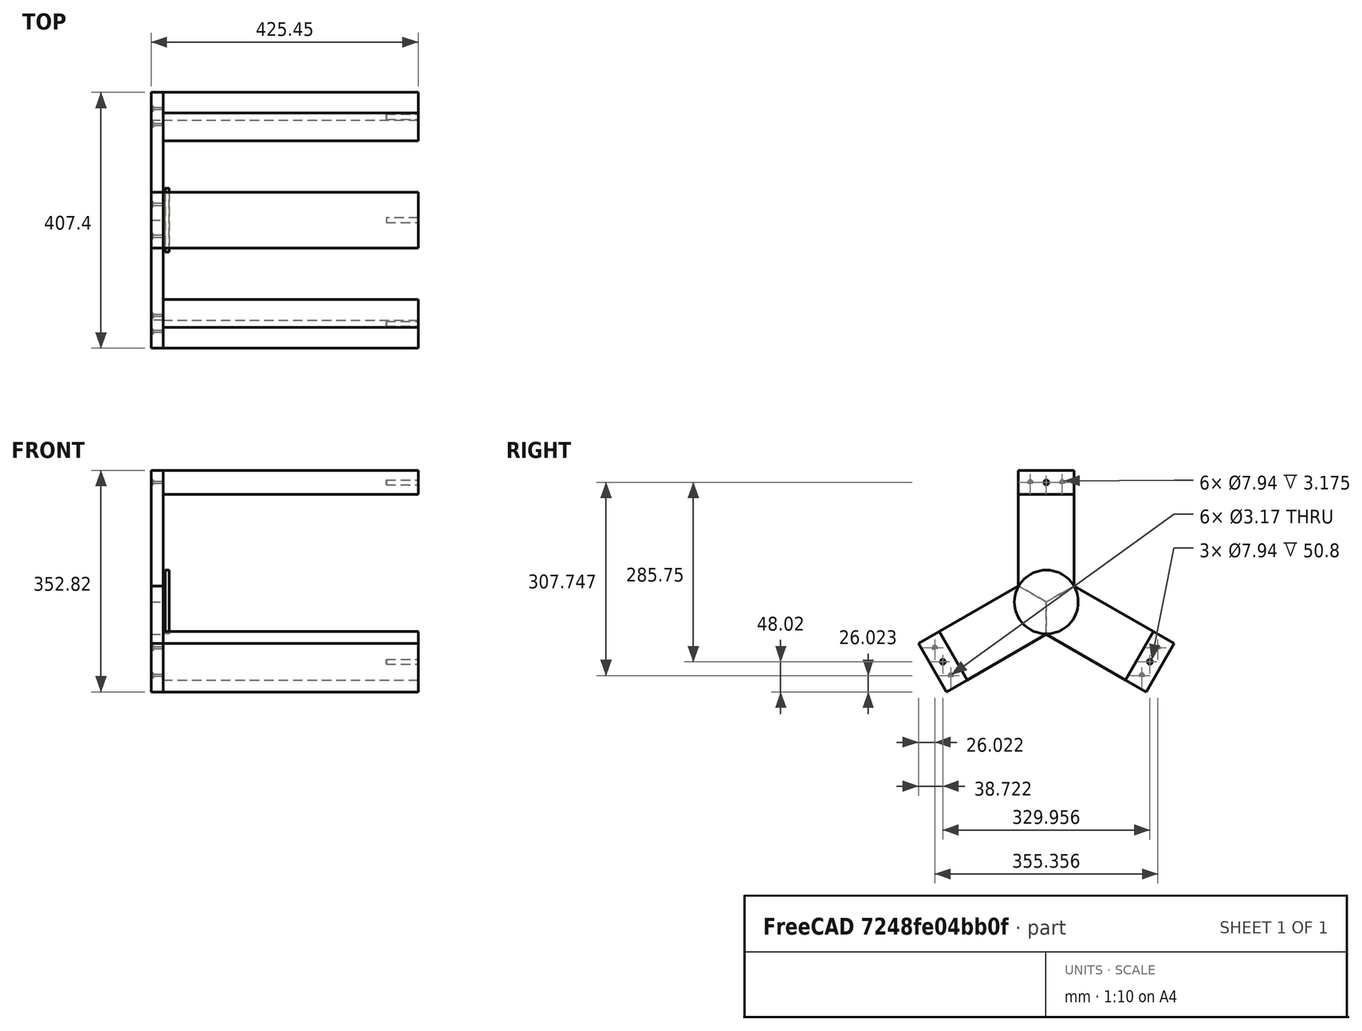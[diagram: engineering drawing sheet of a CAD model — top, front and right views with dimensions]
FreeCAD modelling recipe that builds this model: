
FCSTD DOCUMENT  (FreeCAD 0.20RUnknown)
Label: base
License: All rights reserved
LicenseURL: http://en.wikipedia.org/wiki/All_rights_reserved
objects: Sketcher::SketchObject×19, PartDesign::Pocket×12, PartDesign::Pad×7, PartDesign::Body×7, TechDraw::DrawViewDimension×4, TechDraw::DrawProjGroupItem×2, TechDraw::DrawSVGTemplate×1, TechDraw::DrawProjGroup×1, TechDraw::DrawPage×1, App::Part×1
note: 64 computed .brp shape members not serialized (recipe doc carries the construction recipe); baked Part::Feature solids carry a one-line shape summary decoded from their .brp

FEATURE [Sketcher::SketchObject] Sketch155
  FullyConstrained = true
  MapMode = 5
  Placement = pos=(0,0,0) rot=(0.57735,0.57735,0.57735;2.0944rad)
  Support = -> [YZ_Plane061]
  sketch-geometry (5):
    g0: LineSegment StartX=44.45 StartY=209.55 StartZ=0 EndX=44.45 EndY=171.45 EndZ=0
    g1: LineSegment StartX=44.45 StartY=171.45 StartZ=0 EndX=-44.45 EndY=171.45 EndZ=0
    g2: LineSegment StartX=-44.45 StartY=171.45 StartZ=0 EndX=-44.45 EndY=209.55 EndZ=0
    g3: LineSegment StartX=-44.45 StartY=209.55 StartZ=0 EndX=44.45 EndY=209.55 EndZ=0
    g4: GeomPoint X=0 Y=190.5 Z=0
  constraints (13):
    c: Coincident(g0,g1)
    c: Coincident(g1,g2)
    c: Coincident(g2,g3)
    c: Coincident(g3,g0)
    c: Horizontal(g1)
    c: Horizontal(g3)
    c: Vertical(g0)
    c: Vertical(g2)
    c: Symmetric(g1,g0,g4)
    c: PointOnObject(g4,g-2)
    c: Distance(g-1,g4) = 190.5
    c: DistanceX(g3,g3) = 88.9
    c: DistanceY(g2,g2) = 38.1
FEATURE [PartDesign::Pad] Pad052
  Direction = (1,-2e-16,3e-16)
  Length = 406.4
  Length2 = 10
  Placement = pos=(0,0,0) rot=(0.57735,0.57735,0.57735;2.0944rad)
  Profile = -> Sketch155
  ReferenceAxis = -> Sketch155 [N_Axis]
  Type = 0
FEATURE [Sketcher::SketchObject] Sketch157
  FullyConstrained = true
  MapMode = 5
  Placement = pos=(406.4,-8.9e-14,8.9e-14) rot=(0.57735,0.57735,0.57735;2.0944rad)
  sketch-geometry (1):
    g0: Circle CenterX=0 CenterY=190.5 CenterZ=0 NormalX=0 NormalY=0 NormalZ=1 AngleXU=0 Radius=3.96875
  constraints (3):
    c: PointOnObject(g0,g-2)
    c: DistanceY(g-1,g0) = 190.5
    c: Diameter(g0) = 7.9375
FEATURE [PartDesign::Pocket] Pocket013
  BaseFeature = -> Pad052
  Direction = (-1,2e-16,-2e-16)
  Length = 50.8
  Length2 = 5
  Placement = pos=(0,0,0) rot=(0.57735,0.57735,0.57735;2.0944rad)
  Profile = -> Sketch157
  ReferenceAxis = -> Sketch157 [N_Axis]
  Type = 0
FEATURE [PartDesign::Body] Body050  label="base-leg-001"
  Group = -> [Sketch155,Pad052,Sketch157,Pocket013]
  Origin = -> Origin061
  Placement = pos=(-841.375,0,0) rot=(1,0,0;0rad)
  Tip = -> Pocket013
FEATURE [Sketcher::SketchObject] Sketch158
  FullyConstrained = true
  MapMode = 5
  Placement = pos=(0,0,0) rot=(0.57735,0.57735,0.57735;2.0944rad)
  Support = -> [YZ_Plane061]
  sketch-geometry (5):
    g0: LineSegment StartX=44.45 StartY=209.55 StartZ=0 EndX=44.45 EndY=171.45 EndZ=0
    g1: LineSegment StartX=44.45 StartY=171.45 StartZ=0 EndX=-44.45 EndY=171.45 EndZ=0
    g2: LineSegment StartX=-44.45 StartY=171.45 StartZ=0 EndX=-44.45 EndY=209.55 EndZ=0
    g3: LineSegment StartX=-44.45 StartY=209.55 StartZ=0 EndX=44.45 EndY=209.55 EndZ=0
    g4: GeomPoint X=0 Y=190.5 Z=0
  constraints (13):
    c: Coincident(g0,g1)
    c: Coincident(g1,g2)
    c: Coincident(g2,g3)
    c: Coincident(g3,g0)
    c: Horizontal(g1)
    c: Horizontal(g3)
    c: Vertical(g0)
    c: Vertical(g2)
    c: Symmetric(g1,g0,g4)
    c: PointOnObject(g4,g-2)
    c: Distance(g-1,g4) = 190.5
    c: DistanceX(g3,g3) = 88.9
    c: DistanceY(g2,g2) = 38.1
FEATURE [PartDesign::Pad] Pad053
  Direction = (1,-2e-16,3e-16)
  Length = 406.4
  Length2 = 10
  Placement = pos=(0,0,0) rot=(0.57735,0.57735,0.57735;2.0944rad)
  Profile = -> Sketch158
  ReferenceAxis = -> Sketch158 [N_Axis]
  Type = 0
FEATURE [Sketcher::SketchObject] Sketch159
  FullyConstrained = true
  MapMode = 5
  Placement = pos=(406.4,-8.9e-14,8.9e-14) rot=(0.57735,0.57735,0.57735;2.0944rad)
  sketch-geometry (1):
    g0: Circle CenterX=0 CenterY=190.5 CenterZ=0 NormalX=0 NormalY=0 NormalZ=1 AngleXU=0 Radius=3.96875
  constraints (3):
    c: PointOnObject(g0,g-2)
    c: DistanceY(g-1,g0) = 190.5
    c: Diameter(g0) = 7.9375
FEATURE [PartDesign::Pocket] Pocket014
  BaseFeature = -> Pad053
  Direction = (-1,2e-16,-2e-16)
  Length = 50.8
  Length2 = 5
  Placement = pos=(0,0,0) rot=(0.57735,0.57735,0.57735;2.0944rad)
  Profile = -> Sketch159
  ReferenceAxis = -> Sketch159 [N_Axis]
  Type = 0
FEATURE [PartDesign::Body] Body051  label="base-leg-002"
  Group = -> [Sketch158,Pad053,Sketch159,Pocket014]
  Origin = -> Origin
  Placement = pos=(-841.375,0,0) rot=(1,0,0;4.18879rad)
  Tip = -> Pocket014
FEATURE [Sketcher::SketchObject] Sketch160
  FullyConstrained = true
  MapMode = 5
  Placement = pos=(0,0,0) rot=(0.57735,0.57735,0.57735;2.0944rad)
  Support = -> [YZ_Plane061]
  sketch-geometry (5):
    g0: LineSegment StartX=44.45 StartY=209.55 StartZ=0 EndX=44.45 EndY=171.45 EndZ=0
    g1: LineSegment StartX=44.45 StartY=171.45 StartZ=0 EndX=-44.45 EndY=171.45 EndZ=0
    g2: LineSegment StartX=-44.45 StartY=171.45 StartZ=0 EndX=-44.45 EndY=209.55 EndZ=0
    g3: LineSegment StartX=-44.45 StartY=209.55 StartZ=0 EndX=44.45 EndY=209.55 EndZ=0
    g4: GeomPoint X=0 Y=190.5 Z=0
  constraints (13):
    c: Coincident(g0,g1)
    c: Coincident(g1,g2)
    c: Coincident(g2,g3)
    c: Coincident(g3,g0)
    c: Horizontal(g1)
    c: Horizontal(g3)
    c: Vertical(g0)
    c: Vertical(g2)
    c: Symmetric(g1,g0,g4)
    c: PointOnObject(g4,g-2)
    c: Distance(g-1,g4) = 190.5
    c: DistanceX(g3,g3) = 88.9
    c: DistanceY(g2,g2) = 38.1
FEATURE [PartDesign::Pad] Pad054
  Direction = (1,-2e-16,3e-16)
  Length = 406.4
  Length2 = 10
  Placement = pos=(0,0,0) rot=(0.57735,0.57735,0.57735;2.0944rad)
  Profile = -> Sketch160
  ReferenceAxis = -> Sketch160 [N_Axis]
  Type = 0
FEATURE [Sketcher::SketchObject] Sketch161
  FullyConstrained = true
  MapMode = 5
  Placement = pos=(406.4,-8.9e-14,8.9e-14) rot=(0.57735,0.57735,0.57735;2.0944rad)
  sketch-geometry (1):
    g0: Circle CenterX=0 CenterY=190.5 CenterZ=0 NormalX=0 NormalY=0 NormalZ=1 AngleXU=0 Radius=3.96875
  constraints (3):
    c: PointOnObject(g0,g-2)
    c: DistanceY(g-1,g0) = 190.5
    c: Diameter(g0) = 7.9375
FEATURE [PartDesign::Pocket] Pocket015
  BaseFeature = -> Pad054
  Direction = (-1,2e-16,-2e-16)
  Length = 50.8
  Length2 = 5
  Placement = pos=(0,0,0) rot=(0.57735,0.57735,0.57735;2.0944rad)
  Profile = -> Sketch161
  ReferenceAxis = -> Sketch161 [N_Axis]
  Type = 0
FEATURE [PartDesign::Body] Body052  label="base-leg-003"
  Group = -> [Sketch160,Pad054,Sketch161,Pocket015]
  Origin = -> Origin062
  Placement = pos=(-841.375,0,0) rot=(1,0,0;2.0944rad)
  Tip = -> Pocket015
FEATURE [Sketcher::SketchObject] Sketch
  FullyConstrained = true
  MapMode = 5
  Support = -> [XY_Plane063]
  sketch-geometry (5):
    g0: LineSegment StartX=-9.525 StartY=-44.45 StartZ=0 EndX=-9.525 EndY=44.45 EndZ=0
    g1: LineSegment StartX=-9.525 StartY=44.45 StartZ=0 EndX=9.525 EndY=44.45 EndZ=0
    g2: LineSegment StartX=9.525 StartY=44.45 StartZ=0 EndX=9.525 EndY=-44.45 EndZ=0
    g3: LineSegment StartX=9.525 StartY=-44.45 StartZ=0 EndX=-9.525 EndY=-44.45 EndZ=0
    g4: GeomPoint X=2e-16 Y=-3e-16 Z=0
  constraints (12):
    c: Coincident(g0,g1)
    c: Coincident(g1,g2)
    c: Coincident(g2,g3)
    c: Coincident(g3,g0)
    c: Horizontal(g1)
    c: Horizontal(g3)
    c: Vertical(g0)
    c: Vertical(g2)
    c: Symmetric(g1,g0,g4)
    c: Coincident(g4,g-1)
    c: DistanceY(g2,g2) = 88.9
    c: DistanceX(g3,g3) = 19.05
FEATURE [PartDesign::Pad] Pad
  Direction = (0,0,1)
  Length = 209.55
  Length2 = 10
  Profile = -> Sketch
  ReferenceAxis = -> Sketch [N_Axis]
  Type = 0
FEATURE [Sketcher::SketchObject] Sketch162
  FullyConstrained = true
  MapMode = 5
  Placement = pos=(-9.525,0,0) rot=(0.57735,-0.57735,-0.57735;2.0944rad)
  Support = -> [Pad]
  sketch-geometry (6):
    g0: LineSegment StartX=0 StartY=0 StartZ=0 EndX=44.45 EndY=25.6632 EndZ=0
    g1: LineSegment StartX=0 StartY=0 StartZ=0 EndX=-44.45 EndY=25.6632 EndZ=0
    g2: LineSegment StartX=-44.45 StartY=25.6632 StartZ=0 EndX=44.45 EndY=25.6632 EndZ=0
    g3: LineSegment StartX=44.45 StartY=25.6632 StartZ=0 EndX=44.45 EndY=0 EndZ=0
    g4: LineSegment StartX=44.45 StartY=0 StartZ=0 EndX=-44.45 EndY=0 EndZ=0
    g5: LineSegment StartX=-44.45 StartY=0 StartZ=0 EndX=-44.45 EndY=25.6632 EndZ=0
  constraints (16):
    c: Coincident(g0,g-1)
    c: Coincident(g1,g0)
    c: Angle(g0,g-2) = 1.0472
    c: Angle(g-2,g1) = 1.0472
    c: Coincident(g2,g3)
    c: Coincident(g3,g4)
    c: Coincident(g4,g5)
    c: Coincident(g5,g2)
    c: Horizontal(g2)
    c: Horizontal(g4)
    c: Vertical(g3)
    c: Vertical(g5)
    c: Coincident(g2,g1)
    c: Coincident(g0,g2)
    c: PointOnObject(g3,g-1)
    c: DistanceX(g4,g4) = 88.9
FEATURE [PartDesign::Pocket] Pocket
  BaseFeature = -> Pad
  Direction = (1,0,0)
  Length = 5
  Length2 = 5
  Profile = -> Sketch162
  ReferenceAxis = -> Sketch162 [N_Axis]
  Type = 1
FEATURE [Sketcher::SketchObject] Sketch163
  ExternalGeometry = -> [Pocket]
  FullyConstrained = true
  MapMode = 5
  Placement = pos=(-9.525,0,0) rot=(0.57735,-0.57735,-0.57735;2.0944rad)
  Support = -> [Pocket]
  sketch-geometry (2):
    g0: Circle CenterX=-25.4 CenterY=190.5 CenterZ=0 NormalX=0 NormalY=0 NormalZ=1 AngleXU=0 Radius=1.5875
    g1: Circle CenterX=25.4 CenterY=190.5 CenterZ=0 NormalX=0 NormalY=0 NormalZ=1 AngleXU=0 Radius=1.5875
  constraints (6):
    c: Equal(g1,g0)
    c: DistanceX(g-4,g0) = 19.05
    c: DistanceX(g1,g-5) = 19.05
    c: DistanceY(g1,g-5) = 19.05
    c: DistanceY(g0,g-4) = 19.05
    c: Diameter(g0) = 3.175
FEATURE [PartDesign::Pocket] Pocket016
  BaseFeature = -> Pocket
  Direction = (1,0,0)
  Length = 5
  Length2 = 5
  Profile = -> Sketch163
  ReferenceAxis = -> Sketch163 [N_Axis]
  Type = 1
FEATURE [Sketcher::SketchObject] Sketch164
  ExternalGeometry = -> [Pocket016]
  FullyConstrained = true
  MapMode = 5
  Placement = pos=(-9.525,0,0) rot=(0.57735,-0.57735,-0.57735;2.0944rad)
  Support = -> [Pocket016]
  sketch-geometry (2):
    g0: Circle CenterX=-25.4 CenterY=190.5 CenterZ=0 NormalX=0 NormalY=0 NormalZ=1 AngleXU=0 Radius=3.96875
    g1: Circle CenterX=25.4 CenterY=190.5 CenterZ=0 NormalX=0 NormalY=0 NormalZ=1 AngleXU=0 Radius=3.96875
  constraints (4):
    c: Coincident(g0,g-4)
    c: Coincident(g1,g-3)
    c: Equal(g1,g0)
    c: Diameter(g1) = 7.9375
FEATURE [PartDesign::Pocket] Pocket017
  BaseFeature = -> Pocket016
  Direction = (1,0,0)
  Length = 3.175
  Length2 = 5
  Profile = -> Sketch164
  ReferenceAxis = -> Sketch164 [N_Axis]
  Type = 0
FEATURE [PartDesign::Body] Body  label="base-leg-brace-001"
  Group = -> [Sketch,Pad,Sketch162,Pocket,Sketch163,Pocket016,Sketch164,Pocket017]
  Origin = -> Origin063
  Placement = pos=(-850.9,0,0) rot=(1,0,0;0rad)
  Tip = -> Pocket017
FEATURE [Sketcher::SketchObject] Sketch165
  FullyConstrained = true
  MapMode = 5
  Support = -> [XY_Plane063]
  sketch-geometry (5):
    g0: LineSegment StartX=-9.525 StartY=-44.45 StartZ=0 EndX=-9.525 EndY=44.45 EndZ=0
    g1: LineSegment StartX=-9.525 StartY=44.45 StartZ=0 EndX=9.525 EndY=44.45 EndZ=0
    g2: LineSegment StartX=9.525 StartY=44.45 StartZ=0 EndX=9.525 EndY=-44.45 EndZ=0
    g3: LineSegment StartX=9.525 StartY=-44.45 StartZ=0 EndX=-9.525 EndY=-44.45 EndZ=0
    g4: GeomPoint X=2e-16 Y=-3e-16 Z=0
  constraints (12):
    c: Coincident(g0,g1)
    c: Coincident(g1,g2)
    c: Coincident(g2,g3)
    c: Coincident(g3,g0)
    c: Horizontal(g1)
    c: Horizontal(g3)
    c: Vertical(g0)
    c: Vertical(g2)
    c: Symmetric(g1,g0,g4)
    c: Coincident(g4,g-1)
    c: DistanceY(g2,g2) = 88.9
    c: DistanceX(g3,g3) = 19.05
FEATURE [PartDesign::Pad] Pad055
  Direction = (0,0,1)
  Length = 209.55
  Length2 = 10
  Profile = -> Sketch165
  ReferenceAxis = -> Sketch165 [N_Axis]
  Type = 0
FEATURE [Sketcher::SketchObject] Sketch166
  FullyConstrained = true
  MapMode = 5
  Placement = pos=(-9.525,0,0) rot=(0.57735,-0.57735,-0.57735;2.0944rad)
  Support = -> [Pad055]
  sketch-geometry (6):
    g0: LineSegment StartX=0 StartY=0 StartZ=0 EndX=44.45 EndY=25.6632 EndZ=0
    g1: LineSegment StartX=0 StartY=0 StartZ=0 EndX=-44.45 EndY=25.6632 EndZ=0
    g2: LineSegment StartX=-44.45 StartY=25.6632 StartZ=0 EndX=44.45 EndY=25.6632 EndZ=0
    g3: LineSegment StartX=44.45 StartY=25.6632 StartZ=0 EndX=44.45 EndY=0 EndZ=0
    g4: LineSegment StartX=44.45 StartY=0 StartZ=0 EndX=-44.45 EndY=0 EndZ=0
    g5: LineSegment StartX=-44.45 StartY=0 StartZ=0 EndX=-44.45 EndY=25.6632 EndZ=0
  constraints (16):
    c: Coincident(g0,g-1)
    c: Coincident(g1,g0)
    c: Angle(g0,g-2) = 1.0472
    c: Angle(g-2,g1) = 1.0472
    c: Coincident(g2,g3)
    c: Coincident(g3,g4)
    c: Coincident(g4,g5)
    c: Coincident(g5,g2)
    c: Horizontal(g2)
    c: Horizontal(g4)
    c: Vertical(g3)
    c: Vertical(g5)
    c: Coincident(g2,g1)
    c: Coincident(g0,g2)
    c: PointOnObject(g3,g-1)
    c: DistanceX(g4,g4) = 88.9
FEATURE [PartDesign::Pocket] Pocket018
  BaseFeature = -> Pad055
  Direction = (1,0,0)
  Length = 5
  Length2 = 5
  Profile = -> Sketch166
  ReferenceAxis = -> Sketch166 [N_Axis]
  Type = 1
FEATURE [Sketcher::SketchObject] Sketch167
  ExternalGeometry = -> [Pocket018]
  FullyConstrained = true
  MapMode = 5
  Placement = pos=(-9.525,0,0) rot=(0.57735,-0.57735,-0.57735;2.0944rad)
  Support = -> [Pocket018]
  sketch-geometry (2):
    g0: Circle CenterX=-25.4 CenterY=190.5 CenterZ=0 NormalX=0 NormalY=0 NormalZ=1 AngleXU=0 Radius=1.5875
    g1: Circle CenterX=25.4 CenterY=190.5 CenterZ=0 NormalX=0 NormalY=0 NormalZ=1 AngleXU=0 Radius=1.5875
  constraints (6):
    c: Equal(g1,g0)
    c: DistanceX(g-4,g0) = 19.05
    c: DistanceX(g1,g-5) = 19.05
    c: DistanceY(g1,g-5) = 19.05
    c: DistanceY(g0,g-4) = 19.05
    c: Diameter(g0) = 3.175
FEATURE [PartDesign::Pocket] Pocket019
  BaseFeature = -> Pocket018
  Direction = (1,0,0)
  Length = 5
  Length2 = 5
  Profile = -> Sketch167
  ReferenceAxis = -> Sketch167 [N_Axis]
  Type = 1
FEATURE [Sketcher::SketchObject] Sketch168
  ExternalGeometry = -> [Pocket019]
  FullyConstrained = true
  MapMode = 5
  Placement = pos=(-9.525,0,0) rot=(0.57735,-0.57735,-0.57735;2.0944rad)
  Support = -> [Pocket019]
  sketch-geometry (2):
    g0: Circle CenterX=-25.4 CenterY=190.5 CenterZ=0 NormalX=0 NormalY=0 NormalZ=1 AngleXU=0 Radius=3.96875
    g1: Circle CenterX=25.4 CenterY=190.5 CenterZ=0 NormalX=0 NormalY=0 NormalZ=1 AngleXU=0 Radius=3.96875
  constraints (4):
    c: Coincident(g0,g-4)
    c: Coincident(g1,g-3)
    c: Equal(g1,g0)
    c: Diameter(g1) = 7.9375
FEATURE [PartDesign::Pocket] Pocket020
  BaseFeature = -> Pocket019
  Direction = (1,0,0)
  Length = 3.175
  Length2 = 5
  Profile = -> Sketch168
  ReferenceAxis = -> Sketch168 [N_Axis]
  Type = 0
FEATURE [PartDesign::Body] Body053  label="base-leg-brace-002"
  Group = -> [Sketch165,Pad055,Sketch166,Pocket018,Sketch167,Pocket019,Sketch168,Pocket020]
  Origin = -> Origin064
  Placement = pos=(-850.9,0,0) rot=(1,0,0;2.0944rad)
  Tip = -> Pocket020
FEATURE [Sketcher::SketchObject] Sketch169
  FullyConstrained = true
  MapMode = 5
  Support = -> [XY_Plane063]
  sketch-geometry (5):
    g0: LineSegment StartX=-9.525 StartY=-44.45 StartZ=0 EndX=-9.525 EndY=44.45 EndZ=0
    g1: LineSegment StartX=-9.525 StartY=44.45 StartZ=0 EndX=9.525 EndY=44.45 EndZ=0
    g2: LineSegment StartX=9.525 StartY=44.45 StartZ=0 EndX=9.525 EndY=-44.45 EndZ=0
    g3: LineSegment StartX=9.525 StartY=-44.45 StartZ=0 EndX=-9.525 EndY=-44.45 EndZ=0
    g4: GeomPoint X=2e-16 Y=-3e-16 Z=0
  constraints (12):
    c: Coincident(g0,g1)
    c: Coincident(g1,g2)
    c: Coincident(g2,g3)
    c: Coincident(g3,g0)
    c: Horizontal(g1)
    c: Horizontal(g3)
    c: Vertical(g0)
    c: Vertical(g2)
    c: Symmetric(g1,g0,g4)
    c: Coincident(g4,g-1)
    c: DistanceY(g2,g2) = 88.9
    c: DistanceX(g3,g3) = 19.05
FEATURE [PartDesign::Pad] Pad056
  Direction = (0,0,1)
  Length = 209.55
  Length2 = 10
  Profile = -> Sketch169
  ReferenceAxis = -> Sketch169 [N_Axis]
  Type = 0
FEATURE [Sketcher::SketchObject] Sketch170
  FullyConstrained = true
  MapMode = 5
  Placement = pos=(-9.525,0,0) rot=(0.57735,-0.57735,-0.57735;2.0944rad)
  Support = -> [Pad056]
  sketch-geometry (6):
    g0: LineSegment StartX=0 StartY=0 StartZ=0 EndX=44.45 EndY=25.6632 EndZ=0
    g1: LineSegment StartX=0 StartY=0 StartZ=0 EndX=-44.45 EndY=25.6632 EndZ=0
    g2: LineSegment StartX=-44.45 StartY=25.6632 StartZ=0 EndX=44.45 EndY=25.6632 EndZ=0
    g3: LineSegment StartX=44.45 StartY=25.6632 StartZ=0 EndX=44.45 EndY=0 EndZ=0
    g4: LineSegment StartX=44.45 StartY=0 StartZ=0 EndX=-44.45 EndY=0 EndZ=0
    g5: LineSegment StartX=-44.45 StartY=0 StartZ=0 EndX=-44.45 EndY=25.6632 EndZ=0
  constraints (16):
    c: Coincident(g0,g-1)
    c: Coincident(g1,g0)
    c: Angle(g0,g-2) = 1.0472
    c: Angle(g-2,g1) = 1.0472
    c: Coincident(g2,g3)
    c: Coincident(g3,g4)
    c: Coincident(g4,g5)
    c: Coincident(g5,g2)
    c: Horizontal(g2)
    c: Horizontal(g4)
    c: Vertical(g3)
    c: Vertical(g5)
    c: Coincident(g2,g1)
    c: Coincident(g0,g2)
    c: PointOnObject(g3,g-1)
    c: DistanceX(g4,g4) = 88.9
FEATURE [PartDesign::Pocket] Pocket021
  BaseFeature = -> Pad056
  Direction = (1,0,0)
  Length = 5
  Length2 = 5
  Profile = -> Sketch170
  ReferenceAxis = -> Sketch170 [N_Axis]
  Type = 1
FEATURE [Sketcher::SketchObject] Sketch171
  ExternalGeometry = -> [Pocket021]
  FullyConstrained = true
  MapMode = 5
  Placement = pos=(-9.525,0,0) rot=(0.57735,-0.57735,-0.57735;2.0944rad)
  Support = -> [Pocket021]
  sketch-geometry (2):
    g0: Circle CenterX=-25.4 CenterY=190.5 CenterZ=0 NormalX=0 NormalY=0 NormalZ=1 AngleXU=0 Radius=1.5875
    g1: Circle CenterX=25.4 CenterY=190.5 CenterZ=0 NormalX=0 NormalY=0 NormalZ=1 AngleXU=0 Radius=1.5875
  constraints (6):
    c: Equal(g1,g0)
    c: DistanceX(g-4,g0) = 19.05
    c: DistanceX(g1,g-5) = 19.05
    c: DistanceY(g1,g-5) = 19.05
    c: DistanceY(g0,g-4) = 19.05
    c: Diameter(g0) = 3.175
FEATURE [PartDesign::Pocket] Pocket022
  BaseFeature = -> Pocket021
  Direction = (1,0,0)
  Length = 5
  Length2 = 5
  Profile = -> Sketch171
  ReferenceAxis = -> Sketch171 [N_Axis]
  Type = 1
FEATURE [Sketcher::SketchObject] Sketch172
  ExternalGeometry = -> [Pocket022]
  FullyConstrained = true
  MapMode = 5
  Placement = pos=(-9.525,0,0) rot=(0.57735,-0.57735,-0.57735;2.0944rad)
  Support = -> [Pocket022]
  sketch-geometry (2):
    g0: Circle CenterX=-25.4 CenterY=190.5 CenterZ=0 NormalX=0 NormalY=0 NormalZ=1 AngleXU=0 Radius=3.96875
    g1: Circle CenterX=25.4 CenterY=190.5 CenterZ=0 NormalX=0 NormalY=0 NormalZ=1 AngleXU=0 Radius=3.96875
  constraints (4):
    c: Coincident(g0,g-4)
    c: Coincident(g1,g-3)
    c: Equal(g1,g0)
    c: Diameter(g1) = 7.9375
FEATURE [PartDesign::Pocket] Pocket023
  BaseFeature = -> Pocket022
  Direction = (1,0,0)
  Length = 3.175
  Length2 = 5
  Profile = -> Sketch172
  ReferenceAxis = -> Sketch172 [N_Axis]
  Type = 0
FEATURE [PartDesign::Body] Body054  label="base-leg-brace-003"
  Group = -> [Sketch169,Pad056,Sketch170,Pocket021,Sketch171,Pocket022,Sketch172,Pocket023]
  Origin = -> Origin065
  Placement = pos=(-850.9,0,0) rot=(1,0,0;4.18879rad)
  Tip = -> Pocket023
FEATURE [TechDraw::DrawSVGTemplate] Template
  EditableTexts = Designed_by_Name=Designed by Name; Drawing_number=Drawing number; FC-Date=Date; FC-SC=Scale; FC-SH=Sheet; FC-Title=Title; Rev=rev; Subtitle=Subtitle; Weight=Weight
  Height = 210
  Orientation = 1
  Width = 297
FEATURE [TechDraw::DrawProjGroupItem] ProjItem  label="Front"
  CoarseView = false
  Direction = (1,0,0)
  Focus = 100
  HardHidden = false
  IsoCount = 0
  IsoHidden = false
  IsoVisible = true
  LockPosition = true
  Perspective = false
  Rotation = 0
  RotationVector = (0,1,0)
  ScaleType = 2
  SeamHidden = false
  SeamVisible = true
  SmoothHidden = false
  SmoothVisible = true
  Source = -> [Body]
  Type = 0
  X = 0
  XDirection = (0,1,0)
  Y = 0
FEATURE [TechDraw::DrawProjGroupItem] ProjItem001  label="Right"
  CoarseView = false
  Direction = (1e-16,1,0)
  Focus = 100
  HardHidden = false
  IsoCount = 0
  IsoHidden = false
  IsoVisible = true
  LockPosition = false
  Perspective = false
  Rotation = 0
  RotationVector = (1,0,0)
  ScaleType = 2
  SeamHidden = false
  SeamVisible = true
  SmoothHidden = false
  SmoothVisible = true
  Source = -> [Body]
  Type = 2
  X = 59.45
  XDirection = (-1,1e-16,0)
  Y = 0
FEATURE [TechDraw::DrawProjGroup] ProjGroup
  Anchor = -> ProjItem
  AutoDistribute = true
  LockPosition = false
  ProjectionType = 1
  Rotation = 0
  Scale = 0.5
  ScaleType = 0
  Source = -> [Body]
  Views = -> [ProjItem,ProjItem001]
  X = 91.8074
  Y = 132.988
  spacingX = 15
  spacingY = 15
FEATURE [TechDraw::DrawViewDimension] Dimension
  AngleOverride = false
  Arbitrary = false
  ArbitraryTolerances = false
  EqualTolerance = true
  ExtensionAngle = 0
  FormatSpec = %.2w
  FormatSpecOverTolerance = %+.2w
  FormatSpecUnderTolerance = %+.2w
  Inverted = false
  LineAngle = 0
  LockPosition = false
  MeasureType = 1
  OverTolerance = 0
  References2D = -> [ProjItem]
  Rotation = 0
  Scale = 0.5
  ScaleType = 0
  TheoreticalExact = false
  Type = 2
  UnderTolerance = 0
  X = -50.7478
  Y = 0.97773
FEATURE [TechDraw::DrawViewDimension] Dimension001
  AngleOverride = false
  Arbitrary = false
  ArbitraryTolerances = false
  EqualTolerance = true
  ExtensionAngle = 0
  FormatSpec = %.2w
  FormatSpecOverTolerance = %+.2w
  FormatSpecUnderTolerance = %+.2w
  Inverted = false
  LineAngle = 0
  LockPosition = false
  MeasureType = 1
  OverTolerance = 0
  References2D = -> [ProjItem]
  Rotation = 0
  Scale = 0.5
  ScaleType = 0
  TheoreticalExact = false
  Type = 2
  UnderTolerance = 0
  X = 29.9692
  Y = -59.3059
FEATURE [TechDraw::DrawViewDimension] Dimension002
  AngleOverride = false
  Arbitrary = false
  ArbitraryTolerances = false
  EqualTolerance = true
  ExtensionAngle = 0
  FormatSpec = %.2w
  FormatSpecOverTolerance = %+.2w
  FormatSpecUnderTolerance = %+.2w
  Inverted = false
  LineAngle = 0
  LockPosition = false
  MeasureType = 1
  OverTolerance = 0
  References2D = -> [ProjItem]
  Rotation = 0
  Scale = 0.5
  ScaleType = 0
  TheoreticalExact = false
  Type = 1
  UnderTolerance = 0
  X = 35.8272
  Y = -72.9589
FEATURE [TechDraw::DrawViewDimension] Dimension003
  AngleOverride = false
  Arbitrary = false
  ArbitraryTolerances = false
  EqualTolerance = true
  ExtensionAngle = 0
  FormatSpec = %.2w
  FormatSpecOverTolerance = %+.2w
  FormatSpecUnderTolerance = %+.2w
  Inverted = false
  LineAngle = 0
  LockPosition = false
  MeasureType = 1
  OverTolerance = 0
  References2D = -> [ProjItem]
  Rotation = 0
  Scale = 0.5
  ScaleType = 0
  TheoreticalExact = false
  Type = 6
  UnderTolerance = 0
  X = 8.6611
  Y = -32.0461
FEATURE [TechDraw::DrawPage] Page
  KeepUpdated = true
  NextBalloonIndex = 1
  ProjectionType = 1
  Scale = 0.5
  Template = -> Template
  Views = -> [ProjGroup,Dimension,Dimension001,Dimension002,Dimension003]
FEATURE [Sketcher::SketchObject] Sketch173
  FullyConstrained = true
  MapMode = 5
  Placement = pos=(0,0,0) rot=(0.57735,0.57735,0.57735;2.0944rad)
  Support = -> [YZ_Plane066]
  sketch-geometry (1):
    g0: Circle CenterX=0 CenterY=0 CenterZ=0 NormalX=0 NormalY=0 NormalZ=1 AngleXU=0 Radius=50.8
  constraints (2):
    c: Coincident(g0,g-1)
    c: Diameter(g0) = 101.6
FEATURE [PartDesign::Pad] Pad057
  Direction = (1,-2e-16,3e-16)
  Length = 6.35
  Length2 = 10
  Placement = pos=(0,0,0) rot=(0.57735,0.57735,0.57735;2.0944rad)
  Profile = -> Sketch173
  ReferenceAxis = -> Sketch173 [N_Axis]
  Type = 0
FEATURE [PartDesign::Body] Body055  label="gusset-platge"
  Group = -> [Sketch173,Pad057]
  Origin = -> Origin066
  Placement = pos=(-838.2,0,0) rot=(0,0,1;0rad)
  Tip = -> Pad057
FEATURE [App::Part] Part003  label="assy"
  Group = -> [Body050,Body052,Body051,Body,Body053,Body054,Body055]
  Origin = -> Origin050
